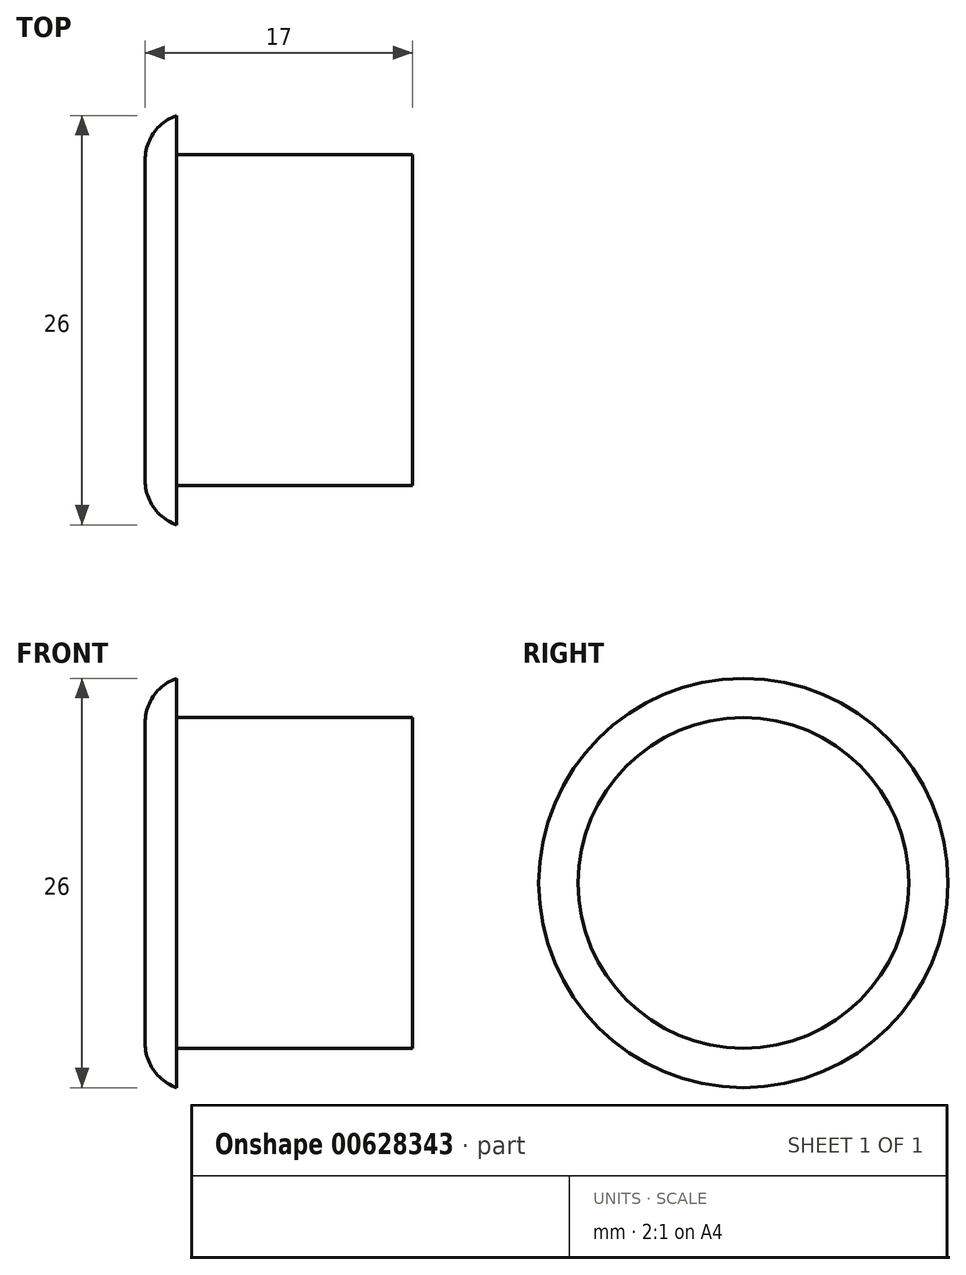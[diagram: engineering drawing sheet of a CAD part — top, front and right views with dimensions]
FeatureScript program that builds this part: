
annotation { "Feature Type Name" : "Feature", "Feature Type Description" : "" }
export const myFeature = defineFeature(function(context is Context, id is Id, definition is map)
    precondition{}
    {
        {
            var Q0;
            Q0=qCreatedBy(makeId("Right.planeOp"),FACE);
            var sketch = newSketch(context, id + "F0", { "sketchPlane" : qUnion([Q0])});
            skCircle(sketch, "E0", {"center": v(0, 0) * mm, "radius": 11 * mm});
            skCircle(sketch, "E1", {"center": v(0, 0) * mm, "radius": 38.5 * mm});
            skSolve(sketch);
        }
        {
            var Q0;
            Q0=makeQuery(id+"F0.imprint","IMPRINT",FACE,{"disambiguationData":[TD([[makeQuery(id+"F0.imprint","IMPRINT",EDGE,{"derivedFrom":sQuery(id+"F0.wireOp",EDGE,"E0")}),1.0]])]});
            var sketch = newSketch(context, id + "F1", { "sketchPlane" : qUnion([Q0])});
            skCircle(sketch, "E2", {"center": v(0, 0) * mm, "radius": 10.5 * mm});
            skCircle(sketch, "E3", {"center": v(0, 0) * mm, "radius": 13 * mm});
            skSolve(sketch);
        }
        {
            var Q0;
            Q0=makeQuery(id+"F1.imprint","IMPRINT",FACE,{"disambiguationData":[TD([[makeQuery(id+"F1.imprint","IMPRINT",EDGE,{"derivedFrom":sQuery(id+"F1.wireOp",EDGE,"E2")}),1.0]])]});
            extrude(context, id + "F2", {"entities" : qUnion([Q0]), "depth" : 15 * mm, "offsetDistance" : 25 * mm});
        }
        {
            var Q0;
            Q0=makeQuery(id+"F0.imprint","IMPRINT",FACE,{"disambiguationData":[TD([[makeQuery(id+"F0.imprint","IMPRINT",EDGE,{"derivedFrom":sQuery(id+"F0.wireOp",EDGE,"E0")}),1.0]])]});
            var sketch = newSketch(context, id + "F3", { "sketchPlane" : qUnion([Q0])});
            skCircle(sketch, "E4", {"center": v(0, 0) * mm, "radius": 13 * mm});
            skSolve(sketch);
        }
        {
            var Q0;
            Q0 = qSketchRegion(id + "F3", true);
            extrude(context, id + "F4", {"entities" : qUnion([Q0]), "operationType" : NewBodyOperationType.ADD, "depth" : -2 * mm, "offsetDistance" : 25 * mm});
        }
        {
            var Q0;
            Q0=makeQuery(id+"F4.opExtrude","CAP_EDGE",EDGE,{"disambiguationData":[OSD([sQuery(id+"F3.wireOp",EDGE,"E4")])],"isStart":false});
            fillet(context, id + "F5", {"entities" : qUnion([Q0]), "radius" : 3 * mm, "tangentPropagation" : true, "allowEdgeOverflow" : false});
        }
    });
